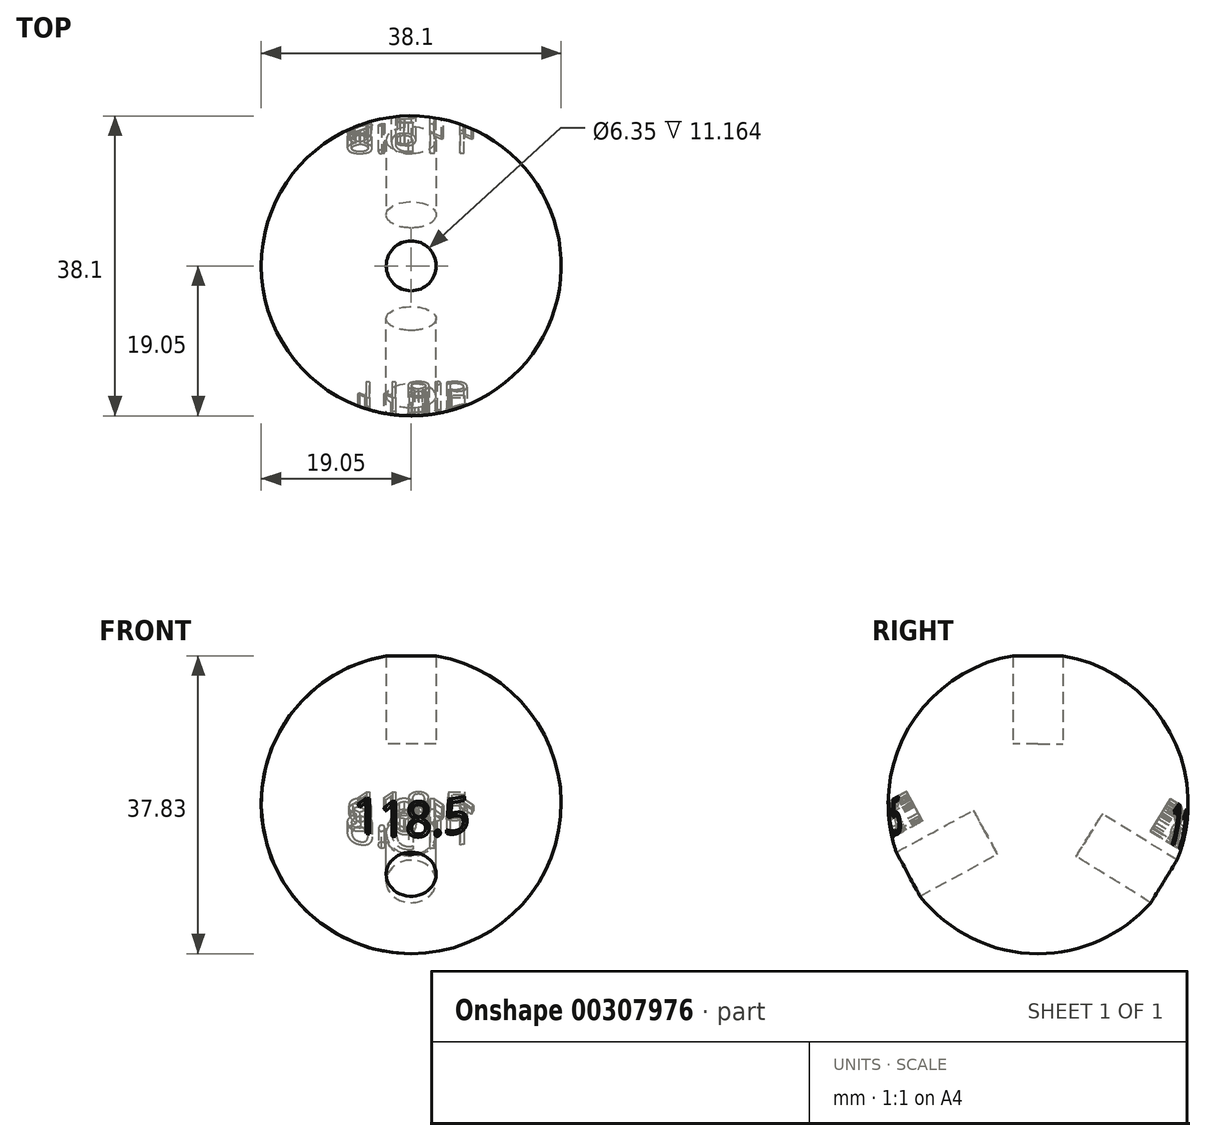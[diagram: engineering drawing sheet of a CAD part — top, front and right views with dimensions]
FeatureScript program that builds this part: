
annotation { "Feature Type Name" : "Feature", "Feature Type Description" : "" }
export const myFeature = defineFeature(function(context is Context, id is Id, definition is map)
    precondition{}
    {
        {
            var Q0;
            Q0=qCreatedBy(makeId("Front.planeOp"),FACE);
            var sketch = newSketch(context, id + "F0", { "sketchPlane" : qUnion([Q0])});
            skArc(sketch, "E0", {"start": v(0, 19.05) * mm, "mid": v(-19.05, 0) * mm, "end": v(0, -19.05) * mm});
            skLineSegment(sketch, "E1", {"start": v(0, 19.05) * mm, "end": v(0, -19.05) * mm});
            skSolve(sketch);
        }
        {
            var Q0;
            Q0=qCreatedBy(makeId("Top.planeOp"),FACE);
            var sketch = newSketch(context, id + "F1", { "sketchPlane" : qUnion([Q0])});
            skCircle(sketch, "E2", {"center": v(0, 0) * mm, "radius": 19.05 * mm});
            skSolve(sketch);
        }
        {
            var Q0;
            Q0=makeQuery(id+"F0.imprint","IMPRINT",FACE,{"disambiguationData":[TD([[makeQuery(id+"F0.imprint","IMPRINT",EDGE,{"derivedFrom":sQuery(id+"F0.wireOp",EDGE,"E0")}),1.0]])]});
            var Q1;
            Q1=sQuery(id+"F1.wireOp",EDGE,"E2");
            revolve(context, id + "F2", {"entities" : qUnion([Q0]), "axis" : qUnion([Q1]), "revolveType" : RevolveType.FULL});
        }
        {
            var Q0;
            Q0=qCreatedBy(makeId("Front.planeOp"),FACE);
            var sketch = newSketch(context, id + "F3", { "sketchPlane" : qUnion([Q0])});
            skLineSegment(sketch, "E3", {"start": v(0, 0) * mm, "end": v(76.32, 0) * mm, "construction": true});
            skLineSegment(sketch, "E4", {"start": v(0, 0) * mm, "end": v(0, 76.7) * mm, "construction": true});
            skSolve(sketch);
        }
        {
            var Q0;
            Q0=qCreatedBy(makeId("Top.planeOp"),FACE);
            cPlane(context, id + "F4", {"entities" : qUnion([Q0]), "cplaneType" : CPlaneType.OFFSET, "offset" : 7.62 * mm, "width" : 152.4 * mm, "height" : 152.4 * mm});
        }
        {
            var Q0;
            Q0=qCreatedBy(id+"F4.planeOp",FACE);
            var sketch = newSketch(context, id + "F5", { "sketchPlane" : qUnion([Q0])});
            skCircle(sketch, "E5", {"center": v(0, 0) * mm, "radius": 3.17 * mm});
            skSolve(sketch);
        }
        {
            var Q0;
            Q0=qSketchRegion(id+"F5",true);
            extrude(context, id + "F6", {"entities" : qUnion([Q0]), "depth" : 76.2 * mm});
        }
        {
            var Q0;
            Q0=makeQuery(id+"F6.opExtrude","SWEPT_BODY",BODY,{"disambiguationData":[OSD([sQuery(id+"F5.wireOp",EDGE,"E5")])]});
            var Q1;
            Q1=sQuery(id+"F3.wireOp",EDGE,"E3");
            transform(context, id + "F7", {"entities" : qUnion([Q0]), "transformType" : TransformType.ROTATION, "transformAxis" : qUnion([Q1]), "angle" : 118.5 * degree, "makeCopy" : true});
        }
        {
            var Q0;
            Q0=makeQuery(id+"F7.opPattern","COPY",BODY,{"derivedFrom":makeQuery(id+"F6.opExtrude","SWEPT_BODY",BODY,{"disambiguationData":[OSD([sQuery(id+"F5.wireOp",EDGE,"E5")])]}),"instanceName":"1"});
            var Q1;
            Q1=sQuery(id+"F3.wireOp",EDGE,"E3");
            transform(context, id + "F8", {"entities" : qUnion([Q0]), "transformType" : TransformType.ROTATION, "transformAxis" : qUnion([Q1]), "angle" : 119.8 * degree, "makeCopy" : true});
        }
        {
            var Q0;
            Q0=makeQuery(id+"F7.opPattern","COPY",FACE,{"derivedFrom":makeQuery(id+"F6.opExtrude","CAP_FACE",FACE,{"disambiguationData":[OSD([sQuery(id+"F5.wireOp",EDGE,"E5")])],"isStart":false}),"instanceName":"1"});
            cPlane(context, id + "F9", {"entities" : qUnion([Q0]), "cplaneType" : CPlaneType.OFFSET, "offset" : 63.5 * mm, "oppositeDirection" : true, "width" : 152.4 * mm, "height" : 152.4 * mm});
        }
        {
            var Q0;
            Q0=qCreatedBy(id+"F9.planeOp",FACE);
            var sketch = newSketch(context, id + "F10", { "sketchPlane" : qUnion([Q0])});
            skText(sketch, "E6", { "text": "118.5\n", "fontName": "OpenSans-Regular.ttf"});
            const initialGuessF10  = {"E6": [-0.00732, 0.00517, 1, 0, 0.00416]};
            skSetInitialGuess(sketch, initialGuessF10);
            skSolve(sketch);
        }
        {
            var Q0;
            Q0=qSketchRegion(id+"F10",true);
            extrude(context, id + "F11", {"entities" : qUnion([Q0]), "operationType" : NewBodyOperationType.REMOVE, "oppositeDirection" : true, "depth" : 6.35 * mm});
        }
        {
            var Q0;
            Q0=makeQuery(id+"F8.opPattern","COPY",FACE,{"derivedFrom":makeQuery(id+"F7.opPattern","COPY",FACE,{"derivedFrom":makeQuery(id+"F6.opExtrude","CAP_FACE",FACE,{"disambiguationData":[OSD([sQuery(id+"F5.wireOp",EDGE,"E5")])],"isStart":false}),"instanceName":"1"}),"instanceName":"1"});
            cPlane(context, id + "F12", {"entities" : qUnion([Q0]), "cplaneType" : CPlaneType.OFFSET, "offset" : 63.5 * mm, "oppositeDirection" : true, "width" : 152.4 * mm, "height" : 152.4 * mm});
        }
        {
            var Q0;
            Q0=qCreatedBy(id+"F12.planeOp",FACE);
            var sketch = newSketch(context, id + "F13", { "sketchPlane" : qUnion([Q0])});
            skText(sketch, "E7", { "text": "119.8", "fontName": "OpenSans-Regular.ttf"});
            const initialGuessF13  = {"E7": [-0.00853, 0.0046, 1, 0, 0.00478]};
            skSetInitialGuess(sketch, initialGuessF13);
            skSolve(sketch);
        }
        {
            var Q0;
            Q0=qSketchRegion(id+"F13",true);
            extrude(context, id + "F14", {"entities" : qUnion([Q0]), "operationType" : NewBodyOperationType.REMOVE, "oppositeDirection" : true, "depth" : 6.35 * mm});
        }
        {
            var Q0;
            Q0=makeQuery(id+"F6.opExtrude","SWEPT_BODY",BODY,{"disambiguationData":[OSD([sQuery(id+"F5.wireOp",EDGE,"E5")])]});
            var Q1;
            Q1=makeQuery(id+"F7.opPattern","COPY",BODY,{"derivedFrom":makeQuery(id+"F6.opExtrude","SWEPT_BODY",BODY,{"disambiguationData":[OSD([sQuery(id+"F5.wireOp",EDGE,"E5")])]}),"instanceName":"1"});
            var Q2;
            Q2=makeQuery(id+"F8.opPattern","COPY",BODY,{"derivedFrom":makeQuery(id+"F7.opPattern","COPY",BODY,{"derivedFrom":makeQuery(id+"F6.opExtrude","SWEPT_BODY",BODY,{"disambiguationData":[OSD([sQuery(id+"F5.wireOp",EDGE,"E5")])]}),"instanceName":"1"}),"instanceName":"1"});
            var Q3;
            Q3=makeQuery(id+"F2.opRevolve","SWEPT_BODY",BODY,{"disambiguationData":[OSD([sQuery(id+"F0.wireOp",EDGE,"E0"),sQuery(id+"F0.wireOp",EDGE,"E1")])]});
            booleanBodies(context, id + "F15", {"operationType" : BooleanOperationType.SUBTRACTION, "tools" : qUnion([Q0, Q1, Q2]), "targets" : qUnion([Q3])});
        }
    });
